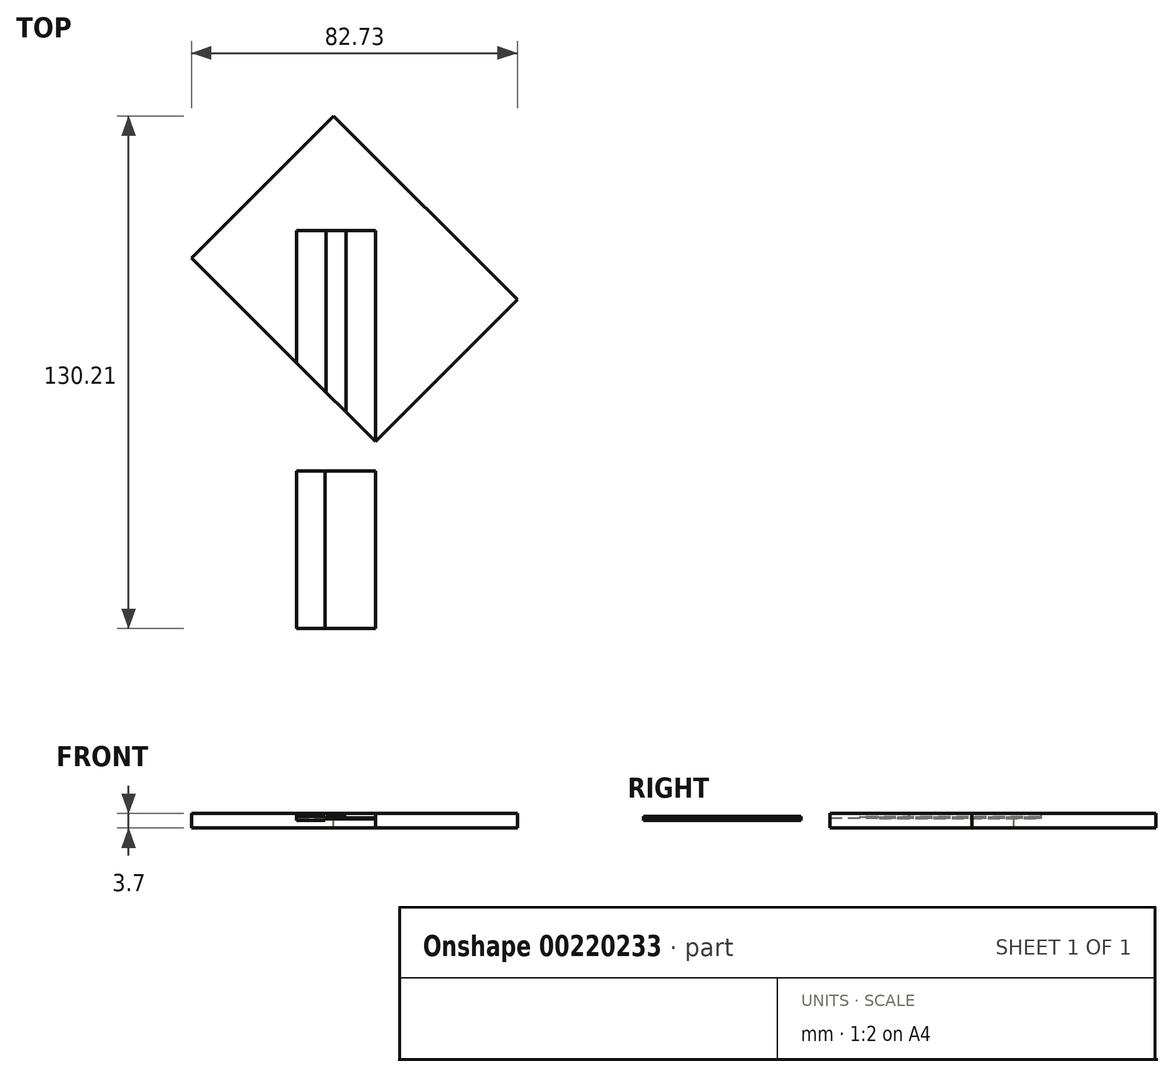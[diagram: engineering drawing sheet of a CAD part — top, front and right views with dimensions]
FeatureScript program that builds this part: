
annotation { "Feature Type Name" : "Feature", "Feature Type Description" : "" }
export const myFeature = defineFeature(function(context is Context, id is Id, definition is map)
    precondition{}
    {
        {
            var Q0;
            Q0=qCreatedBy(makeId("Top.planeOp"),FACE);
            var sketch = newSketch(context, id + "F0", { "sketchPlane" : qUnion([Q0])});
            skLineSegment(sketch, "E0", {"start": v(-51.56, 51.56) * mm, "end": v(43.58, -43.58) * mm, "construction": true});
            skLineSegment(sketch, "E1", {"start": v(0, 38.86) * mm, "end": v(0, -42.15) * mm, "construction": true});
            skLineSegment(sketch, "E2", {"start": v(0, 62.81) * mm, "end": v(0, -62.33) * mm, "construction": true});
            skLineSegment(sketch, "E3", {"start": v(-20, 65.53) * mm, "end": v(-20, -61.98) * mm, "construction": true});
            skLineSegment(sketch, "E4", {"start": v(-61.66, 46.1) * mm, "end": v(33.42, -48.97) * mm, "construction": true});
            skLineSegment(sketch, "E5", {"start": v(-45.9, 38) * mm, "end": v(25.07, 38) * mm, "construction": true});
            skLineSegment(sketch, "E6", {"start": v(-47.15, -2) * mm, "end": v(34.3, -2) * mm, "construction": true});
            skLineSegment(sketch, "E7", {"start": v(-53.2, 56.17) * mm, "end": v(41.32, -38.35) * mm, "construction": true});
            skSolve(sketch);
        }
        {
            var Q0;
            Q0=qCreatedBy(makeId("Top.planeOp"),FACE);
            var sketch = newSketch(context, id + "F1", { "sketchPlane" : qUnion([Q0])});
            skLineSegment(sketch, "E8.bottom", {"start": v(-20, -23.03) * mm, "end": v(-12.8, -23.03) * mm});
            skLineSegment(sketch, "E8.top", {"start": v(-20, -63.03) * mm, "end": v(-12.8, -63.03) * mm});
            skLineSegment(sketch, "E8.left", {"start": v(-20, -23.03) * mm, "end": v(-20, -63.03) * mm});
            skLineSegment(sketch, "E8.right", {"start": v(-12.8, -23.03) * mm, "end": v(-12.8, -63.03) * mm});
            skSolve(sketch);
        }
        {
            var Q0;
            Q0=qCreatedBy(makeId("Top.planeOp"),FACE);
            var sketch = newSketch(context, id + "F2", { "sketchPlane" : qUnion([Q0])});
            skLineSegment(sketch, "E9.bottom", {"start": v(-12.8, -23.03) * mm, "end": v(0, -23.03) * mm});
            skLineSegment(sketch, "E9.top", {"start": v(-12.8, -63.03) * mm, "end": v(0, -63.03) * mm});
            skLineSegment(sketch, "E9.left", {"start": v(-12.8, -23.03) * mm, "end": v(-12.8, -63.03) * mm});
            skLineSegment(sketch, "E9.right", {"start": v(0, -23.03) * mm, "end": v(0, -63.03) * mm});
            skSolve(sketch);
        }
        {
            var Q0;
            Q0=makeQuery(id+"F1.imprint","IMPRINT",FACE,{"disambiguationData":[TD([[makeQuery(id+"F1.imprint","IMPRINT",EDGE,{"derivedFrom":sQuery(id+"F1.wireOp",EDGE,"E8.bottom")}),-1.0]])]});
            extrude(context, id + "F3", {"entities" : qUnion([Q0]), "depth" : .5 * mm, "hasSecondDirection" : true, "secondDirectionOppositeDirection" : true, "secondDirectionDepth" : .5 * mm});
        }
        {
            var Q0;
            Q0=qSketchRegion(id+"F2",true);
            extrude(context, id + "F4", {"entities" : qUnion([Q0]), "operationType" : NewBodyOperationType.ADD, "depth" : .125 * mm, "hasSecondDirection" : true, "secondDirectionOppositeDirection" : true, "secondDirectionDepth" : .125 * mm});
        }
        {
            var Q0;
            Q0=qCreatedBy(makeId("Top.planeOp"),FACE);
            var sketch = newSketch(context, id + "F5", { "sketchPlane" : qUnion([Q0])});
            skLineSegment(sketch, "E10.bottom", {"start": v(-46.83, 31.28) * mm, "end": v(0, -15.56) * mm});
            skLineSegment(sketch, "E10.top", {"start": v(-10.6, 67.18) * mm, "end": v(36.06, 20.5) * mm});
            skLineSegment(sketch, "E10.left", {"start": v(-46.67, 31.11) * mm, "end": v(-10.6, 67.18) * mm});
            skLineSegment(sketch, "E10.right", {"start": v(0, -15.56) * mm, "end": v(36.06, 20.5) * mm});
            skSolve(sketch);
        }
        {
            var Q0;
            Q0=qSketchRegion(id+"F5",true);
            extrude(context, id + "F6", {"entities" : qUnion([Q0]), "oppositeDirection" : true, "depth" : 2.4 * mm, "hasSecondDirection" : true, "secondDirectionOppositeDirection" : false, "secondDirectionDepth" : 1.3 * mm});
        }
        {
            var Q0;
            Q0=qCreatedBy(makeId("Top.planeOp"),FACE);
            var sketch = newSketch(context, id + "F7", { "sketchPlane" : qUnion([Q0])});
            skLineSegment(sketch, "E11", {"start": v(0, 38) * mm, "end": v(-20, 38) * mm});
            skLineSegment(sketch, "E12", {"start": v(-20, 38) * mm, "end": v(-20, 4.44) * mm});
            skLineSegment(sketch, "E13", {"start": v(-20, 4.44) * mm, "end": v(0, -15.56) * mm});
            skLineSegment(sketch, "E14", {"start": v(0, 38) * mm, "end": v(0, -15.56) * mm});
            skPoint(sketch, "E15", {"position": v(0, -15.56) * mm});
            skSolve(sketch);
        }
        {
            var Q0;
            Q0 = qSketchRegion(id + "F7", true);
            extrude(context, id + "F8", {"entities" : qUnion([Q0]), "operationType" : NewBodyOperationType.REMOVE, "depth" : 1.3 * mm});
        }
        {
            var Q0;
            Q0=qCreatedBy(makeId("Top.planeOp"),FACE);
            var sketch = newSketch(context, id + "F9", { "sketchPlane" : qUnion([Q0])});
            skLineSegment(sketch, "E16", {"start": v(-12.5, 38) * mm, "end": v(-7.5, 38) * mm});
            skLineSegment(sketch, "E17", {"start": v(-7.5, 38) * mm, "end": v(-7.5, -8.06) * mm});
            skLineSegment(sketch, "E18", {"start": v(-7.5, -8.06) * mm, "end": v(-12.5, -3.06) * mm});
            skLineSegment(sketch, "E19", {"start": v(-12.5, -3.06) * mm, "end": v(-12.5, 38) * mm});
            skSolve(sketch);
        }
        {
            var Q0;
            Q0=qSketchRegion(id+"F9",true);
            extrude(context, id + "F10", {"entities" : qUnion([Q0]), "operationType" : NewBodyOperationType.ADD, "depth" : .4 * mm});
        }
    });
